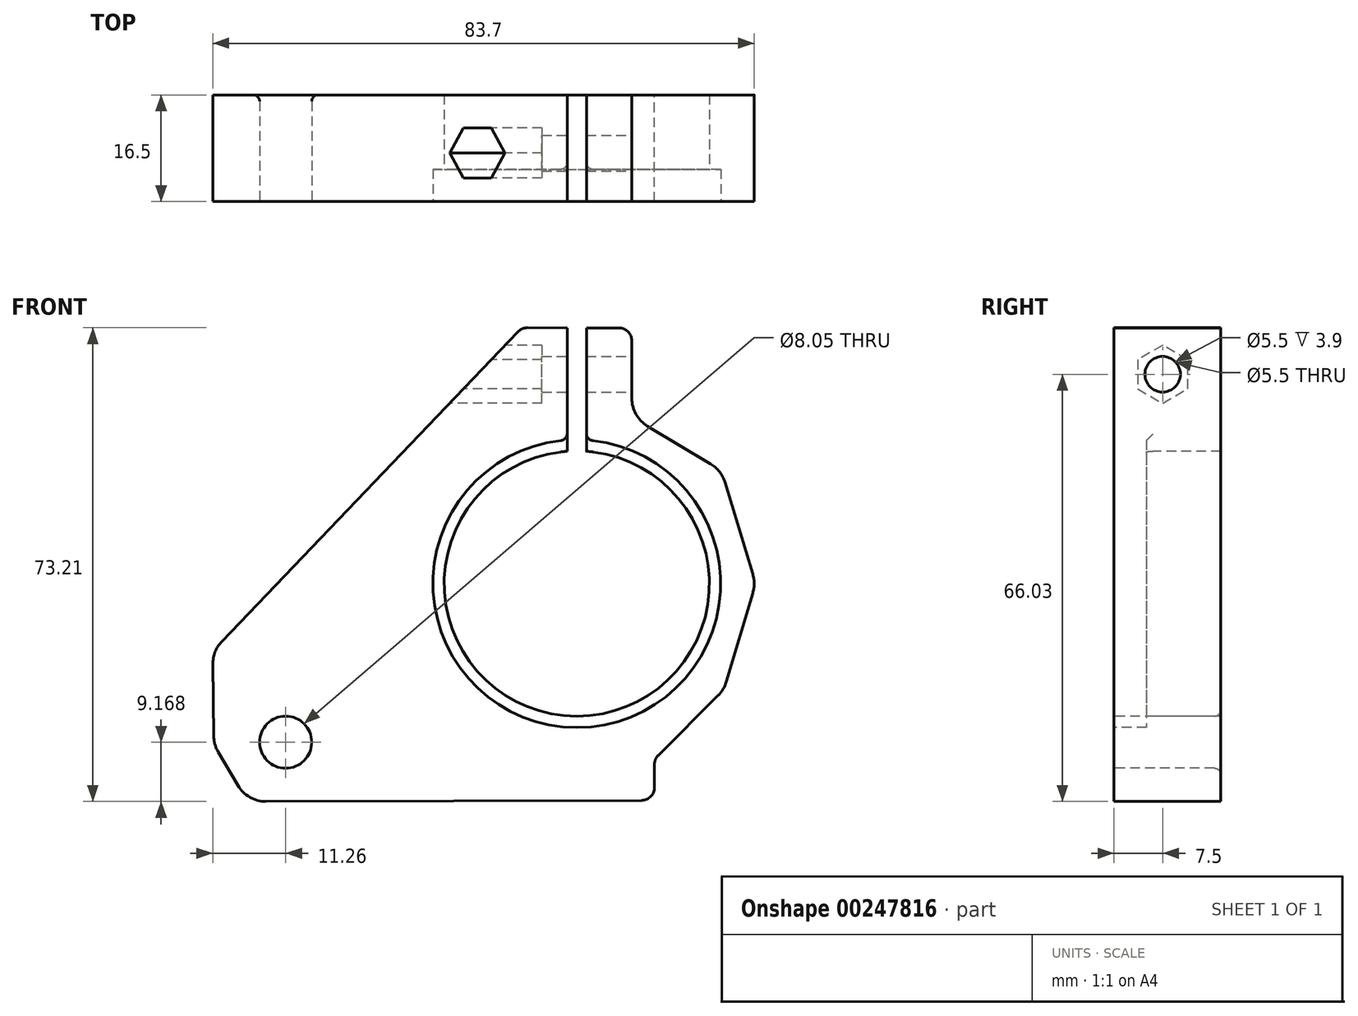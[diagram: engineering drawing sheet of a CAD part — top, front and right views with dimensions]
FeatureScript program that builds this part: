
annotation { "Feature Type Name" : "Feature", "Feature Type Description" : "" }
export const myFeature = defineFeature(function(context is Context, id is Id, definition is map)
    precondition{}
    {
        {
            var Q0;
            Q0=qCreatedBy(makeId("Front.planeOp"),FACE);
            var sketch = newSketch(context, id + "F0", { "sketchPlane" : qUnion([Q0])});
            skCircle(sketch, "E0", {"center": v(0, 0) * mm, "radius": 20.5 * mm});
            skSolve(sketch);
        }
        {
            var Q0;
            Q0=qCreatedBy(makeId("Front.planeOp"),FACE);
            var sketch = newSketch(context, id + "F1", { "sketchPlane" : qUnion([Q0])});
            skCircle(sketch, "E1", {"center": v(0, 0) * mm, "radius": 25.5 * mm});
            skSolve(sketch);
        }
        {
            var Q0;
            Q0=qCreatedBy(makeId("Front.planeOp"),FACE);
            var sketch = newSketch(context, id + "F2", { "sketchPlane" : qUnion([Q0])});
            skLineSegment(sketch, "E2.bottom", {"start": v(0, 39.5) * mm, "end": v(8.5, 39.5) * mm});
            skLineSegment(sketch, "E2.top", {"start": v(0, 20.5) * mm, "end": v(8.5, 20.5) * mm});
            skLineSegment(sketch, "E2.left", {"start": v(0, 39.5) * mm, "end": v(0, 20.5) * mm});
            skLineSegment(sketch, "E2.right", {"start": v(8.5, 39.5) * mm, "end": v(8.5, 20.5) * mm});
            skSolve(sketch);
        }
        {
            var Q0;
            Q0=qCreatedBy(makeId("Front.planeOp"),FACE);
            var sketch = newSketch(context, id + "F3", { "sketchPlane" : qUnion([Q0])});
            skLineSegment(sketch, "E3", {"start": v(-82.14, -33.5) * mm, "end": v(83.47, -33.5) * mm, "construction": true});
            skSolve(sketch);
        }
        {
            var Q0;
            Q0=qCreatedBy(makeId("Front.planeOp"),FACE);
            var sketch = newSketch(context, id + "F4", { "sketchPlane" : qUnion([Q0])});
            skLineSegment(sketch, "E4", {"start": v(12, 14.57) * mm, "end": v(12, -33.5) * mm, "construction": true});
            skSolve(sketch);
        }
        {
            var Q0;
            Q0=qCreatedBy(makeId("Front.planeOp"),FACE);
            var sketch = newSketch(context, id + "F5", { "sketchPlane" : qUnion([Q0])});
            skLineSegment(sketch, "E5", {"start": v(-54, 24.36) * mm, "end": v(-54, -39.87) * mm, "construction": true});
            skSolve(sketch);
        }
        {
            var Q0;
            Q0=qCreatedBy(makeId("Front.planeOp"),FACE);
            var sketch = newSketch(context, id + "F6", { "sketchPlane" : qUnion([Q0])});
            skLineSegment(sketch, "E6", {"start": v(-54, -28.5) * mm, "end": v(30.8, -28.5) * mm, "construction": true});
            skSolve(sketch);
        }
        {
            var Q0;
            Q0=qCreatedBy(makeId("Front.planeOp"),FACE);
            var sketch = newSketch(context, id + "F7", { "sketchPlane" : qUnion([Q0])});
            skLineSegment(sketch, "E7", {"start": v(-49, 18.78) * mm, "end": v(-49, -35.89) * mm, "construction": true});
            skSolve(sketch);
        }
        {
            var Q0;
            Q0=qCreatedBy(makeId("Front.planeOp"),FACE);
            var sketch = newSketch(context, id + "F8", { "sketchPlane" : qUnion([Q0])});
            skLineSegment(sketch, "E8", {"start": v(-49, -24.5) * mm, "end": v(12.95, -24.5) * mm, "construction": true});
            skSolve(sketch);
        }
        {
            var Q0;
            Q0=qCreatedBy(makeId("Front.planeOp"),FACE);
            var sketch = newSketch(context, id + "F9", { "sketchPlane" : qUnion([Q0])});
            skCircle(sketch, "E9", {"center": v(-45.01, -24.5) * mm, "radius": 4 * mm, "construction": true});
            skSolve(sketch);
        }
        {
            var Q0;
            Q0=qCreatedBy(makeId("Front.planeOp"),FACE);
            var sketch = newSketch(context, id + "F10", { "sketchPlane" : qUnion([Q0])});
            skCircle(sketch, "E10", {"center": v(-45.01, -24.5) * mm, "radius": 9 * mm, "construction": true});
            skSolve(sketch);
        }
        {
            var Q0;
            Q0=qCreatedBy(makeId("Front.planeOp"),FACE);
            var sketch = newSketch(context, id + "F11", { "sketchPlane" : qUnion([Q0])});
            skLineSegment(sketch, "E11", {"start": v(-44.9, -33.5) * mm, "end": v(12.01, -33.5) * mm, "construction": true});
            skLineSegment(sketch, "E12", {"start": v(12.01, -33.5) * mm, "end": v(12.01, -22.5) * mm});
            skSolve(sketch);
        }
        {
            assignVariable(context, id + "F12", {"name" : "grosor", "anyValue" : 15});
        }
        {
            var Q0;
            Q0=qCreatedBy(makeId("Front.planeOp"),FACE);
            cPlane(context, id + "F13", {"entities" : qUnion([Q0]), "cplaneType" : CPlaneType.OFFSET, "offset" : 20 * mm, "width" : 150 * mm, "height" : 150 * mm});
        }
        {
            var Q0;
            Q0=qCreatedBy(id+"F13.planeOp",FACE);
            var sketch = newSketch(context, id + "F14", { "sketchPlane" : qUnion([Q0])});
            skLineSegment(sketch, "E13", {"start": v(-8.5, 39.54) * mm, "end": v(-56.3, -10.43) * mm});
            skLineSegment(sketch, "E14", {"start": v(-56.3, -10.43) * mm, "end": v(-56.12, -24.88) * mm});
            skLineSegment(sketch, "E15", {"start": v(-56.12, -24.88) * mm, "end": v(-50.94, -33.68) * mm});
            skLineSegment(sketch, "E16", {"start": v(-50.94, -33.68) * mm, "end": v(12.01, -33.5) * mm});
            skLineSegment(sketch, "E17", {"start": v(12.01, -33.5) * mm, "end": v(12.01, -27.1) * mm});
            skLineSegment(sketch, "E18", {"start": v(12.01, -27.1) * mm, "end": v(22.74, -16.4) * mm});
            skLineSegment(sketch, "E19", {"start": v(22.74, -16.4) * mm, "end": v(27.65, 0) * mm});
            skLineSegment(sketch, "E20", {"start": v(27.65, 0) * mm, "end": v(22.34, 17.51) * mm});
            skLineSegment(sketch, "E21", {"start": v(22.34, 17.51) * mm, "end": v(8.5, 25.8) * mm});
            skLineSegment(sketch, "E22", {"start": v(8.5, 25.8) * mm, "end": v(8.5, 39.5) * mm});
            skLineSegment(sketch, "E23", {"start": v(8.5, 39.5) * mm, "end": v(-8.5, 39.54) * mm});
            skSolve(sketch);
        }
        {
            var Q0;
            Q0=makeQuery(id+"F14.imprint","IMPRINT",FACE,{"disambiguationData":[TD([[makeQuery(id+"F14.imprint","IMPRINT",EDGE,{"derivedFrom":sQuery(id+"F14.wireOp",EDGE,"E13")}),1.0]])]});
            extrude(context, id + "F15", {"entities" : qUnion([Q0]), "depth" : (getVariable(context, 'grosor') * 1.1) * mm});
        }
        {
            var Q0;
            Q0=makeQuery(id+"F15.opExtrude","CAP_FACE",FACE,{"disambiguationData":[OSD([sQuery(id+"F14.wireOp",EDGE,"E13"),sQuery(id+"F14.wireOp",EDGE,"E14"),sQuery(id+"F14.wireOp",EDGE,"nau9YeAK-7w5c-QdUc-g7JC-ZSVLRHTYuaYn"),sQuery(id+"F14.wireOp",EDGE,"E15"),sQuery(id+"F14.wireOp",EDGE,"E16"),sQuery(id+"F14.wireOp",EDGE,"E17"),sQuery(id+"F14.wireOp",EDGE,"E18"),sQuery(id+"F14.wireOp",EDGE,"E19"),sQuery(id+"F14.wireOp",EDGE,"E20"),sQuery(id+"F14.wireOp",EDGE,"E21"),sQuery(id+"F14.wireOp",EDGE,"E22"),sQuery(id+"F14.wireOp",EDGE,"E23")])],"isStart":false});
            var sketch = newSketch(context, id + "F16", { "sketchPlane" : qUnion([Q0])});
            skCircle(sketch, "E24", {"center": v(0, 0) * mm, "radius": 20.5 * mm});
            skSolve(sketch);
        }
        {
            var Q0;
            Q0=makeQuery(id+"F16.imprint","IMPRINT",FACE,{"disambiguationData":[TD([[makeQuery(id+"F16.imprint","IMPRINT",EDGE,{"derivedFrom":sQuery(id+"F16.wireOp",EDGE,"E24")}),1.0]])]});
            extrude(context, id + "F17", {"entities" : qUnion([Q0]), "operationType" : NewBodyOperationType.REMOVE, "oppositeDirection" : true, "depth" : (getVariable(context, 'grosor') * 1.1) * mm});
        }
        {
            var Q0;
            Q0=makeQuery(id+"F15.opExtrude","CAP_FACE",FACE,{"disambiguationData":[OSD([sQuery(id+"F14.wireOp",EDGE,"E13"),sQuery(id+"F14.wireOp",EDGE,"E14"),sQuery(id+"F14.wireOp",EDGE,"nau9YeAK-7w5c-QdUc-g7JC-ZSVLRHTYuaYn"),sQuery(id+"F14.wireOp",EDGE,"E15"),sQuery(id+"F14.wireOp",EDGE,"E16"),sQuery(id+"F14.wireOp",EDGE,"E17"),sQuery(id+"F14.wireOp",EDGE,"E18"),sQuery(id+"F14.wireOp",EDGE,"E19"),sQuery(id+"F14.wireOp",EDGE,"E20"),sQuery(id+"F14.wireOp",EDGE,"E21"),sQuery(id+"F14.wireOp",EDGE,"E22"),sQuery(id+"F14.wireOp",EDGE,"E23")])],"isStart":false});
            var sketch = newSketch(context, id + "F18", { "sketchPlane" : qUnion([Q0])});
            skCircle(sketch, "E25", {"center": v(-45.02, -24.51) * mm, "radius": 4.03 * mm});
            skSolve(sketch);
        }
        {
            var Q0;
            Q0=makeQuery(id+"F18.imprint","IMPRINT",FACE,{"disambiguationData":[TD([[makeQuery(id+"F18.imprint","IMPRINT",EDGE,{"derivedFrom":sQuery(id+"F18.wireOp",EDGE,"E25")}),1.0]])]});
            extrude(context, id + "F19", {"entities" : qUnion([Q0]), "operationType" : NewBodyOperationType.REMOVE, "oppositeDirection" : true, "depth" : (getVariable(context, 'grosor') * 1.1) * mm});
        }
        {
            var Q0;
            Q0=makeQuery(id+"F15.opExtrude","CAP_FACE",FACE,{"disambiguationData":[OSD([sQuery(id+"F14.wireOp",EDGE,"E13"),sQuery(id+"F14.wireOp",EDGE,"E14"),sQuery(id+"F14.wireOp",EDGE,"nau9YeAK-7w5c-QdUc-g7JC-ZSVLRHTYuaYn"),sQuery(id+"F14.wireOp",EDGE,"E15"),sQuery(id+"F14.wireOp",EDGE,"E16"),sQuery(id+"F14.wireOp",EDGE,"E17"),sQuery(id+"F14.wireOp",EDGE,"E18"),sQuery(id+"F14.wireOp",EDGE,"E19"),sQuery(id+"F14.wireOp",EDGE,"E20"),sQuery(id+"F14.wireOp",EDGE,"E21"),sQuery(id+"F14.wireOp",EDGE,"E22"),sQuery(id+"F14.wireOp",EDGE,"E23")])],"isStart":false});
            var sketch = newSketch(context, id + "F20", { "sketchPlane" : qUnion([Q0])});
            skLineSegment(sketch, "E26.bottom", {"start": v(1.5, 20.45) * mm, "end": v(-1.5, 20.45) * mm});
            skLineSegment(sketch, "E26.top", {"start": v(1.5, 40.45) * mm, "end": v(-1.5, 40.45) * mm});
            skLineSegment(sketch, "E26.left", {"start": v(1.5, 20.45) * mm, "end": v(1.5, 40.45) * mm});
            skLineSegment(sketch, "E26.right", {"start": v(-1.5, 20.45) * mm, "end": v(-1.5, 40.45) * mm});
            skPoint(sketch, "E26.middle", {"position": v(0, 30.45) * mm});
            skSolve(sketch);
        }
        {
            var Q0;
            Q0 = qSketchRegion(id + "F20", true);
            extrude(context, id + "F21", {"entities" : qUnion([Q0]), "operationType" : NewBodyOperationType.REMOVE, "oppositeDirection" : true, "depth" : (getVariable(context, 'grosor') * 1.1) * mm});
        }
        {
            var Q0;
            Q0=makeQuery(id+"F15.opExtrude","SWEPT_FACE",FACE,{"disambiguationData":[OSD([sQuery(id+"F14.wireOp",EDGE,"E22")])]});
            var sketch = newSketch(context, id + "F22", { "sketchPlane" : qUnion([Q0])});
            skCircle(sketch, "E27", {"center": v(-29, 32.35) * mm, "radius": 2.75 * mm});
            skSolve(sketch);
        }
        {
            var Q0;
            Q0=makeQuery(id+"F22.imprint","IMPRINT",FACE,{"disambiguationData":[TD([[makeQuery(id+"F22.imprint","IMPRINT",EDGE,{"derivedFrom":sQuery(id+"F22.wireOp",EDGE,"E27")}),1.0]])]});
            extrude(context, id + "F23", {"entities" : qUnion([Q0]), "operationType" : NewBodyOperationType.REMOVE, "oppositeDirection" : true, "depth" : 40 * mm});
        }
        {
            var Q0;
            Q0=qCreatedBy(makeId("Right.planeOp"),FACE);
            cPlane(context, id + "F24", {"entities" : qUnion([Q0]), "cplaneType" : CPlaneType.OFFSET, "offset" : 36.7 * mm, "oppositeDirection" : true, "width" : 150 * mm, "height" : 150 * mm});
        }
        {
            var Q0;
            Q0=qCreatedBy(id+"F24.planeOp",FACE);
            var sketch = newSketch(context, id + "F25", { "sketchPlane" : qUnion([Q0])});
            skCircle(sketch, "E28.cCircle", {"center": v(-29, 32.35) * mm, "radius": 3.88 * mm, "construction": true});
            skLineSegment(sketch, "E28.0", {"start": v(-32.88, 30.11) * mm, "end": v(-32.88, 34.59) * mm});
            skLineSegment(sketch, "E28.1", {"start": v(-32.88, 34.59) * mm, "end": v(-29, 36.82) * mm});
            skLineSegment(sketch, "E28.2", {"start": v(-29, 36.82) * mm, "end": v(-25.13, 34.59) * mm});
            skLineSegment(sketch, "E28.3", {"start": v(-25.13, 34.59) * mm, "end": v(-25.13, 30.11) * mm});
            skLineSegment(sketch, "E28.4", {"start": v(-25.12, 30.11) * mm, "end": v(-29, 27.88) * mm});
            skLineSegment(sketch, "E28.5", {"start": v(-29, 27.88) * mm, "end": v(-32.88, 30.11) * mm});
            skPoint(sketch, "E28.0.midPoint", {"position": v(-32.88, 32.35) * mm});
            skSolve(sketch);
        }
        {
            var Q0;
            Q0=makeQuery(id+"F25.imprint","IMPRINT",FACE,{"disambiguationData":[TD([[makeQuery(id+"F25.imprint","IMPRINT",EDGE,{"derivedFrom":sQuery(id+"F25.wireOp",EDGE,"E28.0")}),-1.0]])]});
            var Q1;
            Q1=sQuery(id+"F1.wireOp",EDGE,"E1");
            extrude(context, id + "F26", {"entities" : qUnion([Q0]), "operationType" : NewBodyOperationType.REMOVE, "surfaceEntities" : qUnion([Q1]), "depth" : 31.3 * mm});
        }
        {
            var Q0;
            Q0=makeQuery(id+"F15.opExtrude","CAP_FACE",FACE,{"disambiguationData":[OSD([sQuery(id+"F14.wireOp",EDGE,"E13"),sQuery(id+"F14.wireOp",EDGE,"E14"),sQuery(id+"F14.wireOp",EDGE,"nau9YeAK-7w5c-QdUc-g7JC-ZSVLRHTYuaYn"),sQuery(id+"F14.wireOp",EDGE,"E15"),sQuery(id+"F14.wireOp",EDGE,"E16"),sQuery(id+"F14.wireOp",EDGE,"E17"),sQuery(id+"F14.wireOp",EDGE,"E18"),sQuery(id+"F14.wireOp",EDGE,"E19"),sQuery(id+"F14.wireOp",EDGE,"E20"),sQuery(id+"F14.wireOp",EDGE,"E21"),sQuery(id+"F14.wireOp",EDGE,"E22"),sQuery(id+"F14.wireOp",EDGE,"E23")])],"isStart":false});
            var sketch = newSketch(context, id + "F27", { "sketchPlane" : qUnion([Q0])});
            skCircle(sketch, "E29", {"center": v(0, 0) * mm, "radius": 22.25 * mm});
            skSolve(sketch);
        }
        {
            var Q0;
            Q0 = qSketchRegion(id + "F27", true);
            extrude(context, id + "F28", {"entities" : qUnion([Q0]), "operationType" : NewBodyOperationType.REMOVE, "oppositeDirection" : true, "depth" : 5 * mm});
        }
        {
            var Q0;
            Q0=makeQuery(id+"F19.boolean.opBoolean","COPY",EDGE,{"derivedFrom":makeQuery(id+"F19.opExtrude","CAP_EDGE",EDGE,{"disambiguationData":[OSD([sQuery(id+"F18.wireOp",EDGE,"E25")])],"isStart":true})});
            var Q1;
            Q1=makeQuery(id+"F19.boolean.opBoolean","INTERSECT",EDGE,{"derivedFrom":[makeQuery(id+"F15.opExtrude","CAP_FACE",FACE,{"disambiguationData":[OSD([sQuery(id+"F14.wireOp",EDGE,"E13"),sQuery(id+"F14.wireOp",EDGE,"E14"),sQuery(id+"F14.wireOp",EDGE,"nau9YeAK-7w5c-QdUc-g7JC-ZSVLRHTYuaYn"),sQuery(id+"F14.wireOp",EDGE,"E15"),sQuery(id+"F14.wireOp",EDGE,"E16"),sQuery(id+"F14.wireOp",EDGE,"E17"),sQuery(id+"F14.wireOp",EDGE,"E18"),sQuery(id+"F14.wireOp",EDGE,"E19"),sQuery(id+"F14.wireOp",EDGE,"E20"),sQuery(id+"F14.wireOp",EDGE,"E21"),sQuery(id+"F14.wireOp",EDGE,"E22"),sQuery(id+"F14.wireOp",EDGE,"E23")])],"isStart":true}),makeQuery(id+"F19.opExtrude","SWEPT_FACE",FACE,{"disambiguationData":[OSD([sQuery(id+"F18.wireOp",EDGE,"E25")])]})]});
            fillet(context, id + "F29", {"entities" : qUnion([Q0, Q1]), "radius" : 1 * mm, "tangentPropagation" : true, "allowEdgeOverflow" : false});
        }
        {
            var Q0;
            Q0=makeQuery(id+"F15.opExtrude","SWEPT_EDGE",EDGE,{"disambiguationData":[OSD([sQuery(id+"F14.wireOp",EDGE,"E19"),sQuery(id+"F14.wireOp",EDGE,"E20")])]});
            fillet(context, id + "F30", {"entities" : qUnion([Q0]), "radius" : 5 * mm, "tangentPropagation" : true, "allowEdgeOverflow" : false});
        }
        {
            var Q0;
            Q0=makeQuery(id+"F15.opExtrude","SWEPT_EDGE",EDGE,{"disambiguationData":[OSD([sQuery(id+"F14.wireOp",EDGE,"E20"),sQuery(id+"F14.wireOp",EDGE,"E21")])]});
            fillet(context, id + "F31", {"entities" : qUnion([Q0]), "radius" : 5 * mm, "tangentPropagation" : true, "allowEdgeOverflow" : false});
        }
        {
            var Q0;
            Q0=makeQuery(id+"F15.opExtrude","SWEPT_EDGE",EDGE,{"disambiguationData":[OSD([sQuery(id+"F14.wireOp",EDGE,"E18"),sQuery(id+"F14.wireOp",EDGE,"E19")])]});
            fillet(context, id + "F32", {"entities" : qUnion([Q0]), "radius" : 5 * mm, "tangentPropagation" : true, "allowEdgeOverflow" : false});
        }
        {
            var Q0;
            Q0=makeQuery(id+"F15.opExtrude","SWEPT_EDGE",EDGE,{"disambiguationData":[OSD([sQuery(id+"F14.wireOp",EDGE,"E21"),sQuery(id+"F14.wireOp",EDGE,"E22")])]});
            fillet(context, id + "F33", {"entities" : qUnion([Q0]), "radius" : 5 * mm, "tangentPropagation" : true, "allowEdgeOverflow" : false});
        }
        {
            var Q0;
            Q0=makeQuery(id+"F15.opExtrude","SWEPT_EDGE",EDGE,{"disambiguationData":[OSD([sQuery(id+"F14.wireOp",EDGE,"E15"),sQuery(id+"F14.wireOp",EDGE,"E16")])]});
            var Q1;
            Q1=makeQuery(id+"F15.opExtrude","SWEPT_EDGE",EDGE,{"disambiguationData":[OSD([sQuery(id+"F14.wireOp",EDGE,"E14"),sQuery(id+"F14.wireOp",EDGE,"E15")])]});
            var Q2;
            Q2=makeQuery(id+"F15.opExtrude","SWEPT_EDGE",EDGE,{"disambiguationData":[OSD([sQuery(id+"F14.wireOp",EDGE,"E13"),sQuery(id+"F14.wireOp",EDGE,"E14")])]});
            fillet(context, id + "F34", {"entities" : qUnion([Q0, Q1, Q2]), "radius" : 5 * mm, "tangentPropagation" : true, "allowEdgeOverflow" : false});
        }
        {
            var Q0;
            Q0=makeQuery(id+"F15.opExtrude","SWEPT_EDGE",EDGE,{"disambiguationData":[OSD([sQuery(id+"F14.wireOp",EDGE,"E16"),sQuery(id+"F14.wireOp",EDGE,"E17")])]});
            var Q1;
            Q1=makeQuery(id+"F15.opExtrude","SWEPT_EDGE",EDGE,{"disambiguationData":[OSD([sQuery(id+"F14.wireOp",EDGE,"E17"),sQuery(id+"F14.wireOp",EDGE,"E18")])]});
            fillet(context, id + "F35", {"entities" : qUnion([Q0, Q1]), "radius" : 2 * mm, "tangentPropagation" : true, "allowEdgeOverflow" : false});
        }
        {
            var Q0;
            Q0=makeQuery(id+"F15.opExtrude","SWEPT_EDGE",EDGE,{"disambiguationData":[OSD([sQuery(id+"F14.wireOp",EDGE,"E13"),sQuery(id+"F14.wireOp",EDGE,"E23")])]});
            var Q1;
            Q1=makeQuery(id+"F15.opExtrude","SWEPT_EDGE",EDGE,{"disambiguationData":[OSD([sQuery(id+"F14.wireOp",EDGE,"E22"),sQuery(id+"F14.wireOp",EDGE,"E23")])]});
            fillet(context, id + "F36", {"entities" : qUnion([Q0, Q1]), "radius" : 2 * mm, "tangentPropagation" : true, "allowEdgeOverflow" : false});
        }
        {
            var Q0;
            Q0=makeQuery(id+"F21.boolean.opBoolean","COPY",EDGE,{"derivedFrom":makeQuery(id+"F21.opExtrude","SWEPT_EDGE",EDGE,{"disambiguationData":[OSD([sQuery(id+"F16.wireOp",EDGE,"E24"),sQuery(id+"F20.wireOp",EDGE,"E26.bottom"),sQuery(id+"F20.wireOp",EDGE,"E26.right")])]})});
            var Q1;
            Q1=makeQuery(id+"F28.boolean.opBoolean","INTERSECT",EDGE,{"derivedFrom":[makeQuery(id+"F21.boolean.opBoolean","COPY",FACE,{"derivedFrom":makeQuery(id+"F21.opExtrude","SWEPT_FACE",FACE,{"disambiguationData":[OSD([sQuery(id+"F20.wireOp",EDGE,"E26.right")])]})}),makeQuery(id+"F28.opExtrude","SWEPT_FACE",FACE,{"disambiguationData":[OSD([sQuery(id+"F27.wireOp",EDGE,"E29")])]})]});
            var Q2;
            Q2=makeQuery(id+"F21.boolean.opBoolean","COPY",EDGE,{"derivedFrom":makeQuery(id+"F21.opExtrude","SWEPT_EDGE",EDGE,{"disambiguationData":[OSD([sQuery(id+"F16.wireOp",EDGE,"E24"),sQuery(id+"F20.wireOp",EDGE,"E26.bottom"),sQuery(id+"F20.wireOp",EDGE,"E26.left")])]})});
            var Q3;
            Q3=makeQuery(id+"F28.boolean.opBoolean","INTERSECT",EDGE,{"derivedFrom":[makeQuery(id+"F21.boolean.opBoolean","COPY",FACE,{"derivedFrom":makeQuery(id+"F21.opExtrude","SWEPT_FACE",FACE,{"disambiguationData":[OSD([sQuery(id+"F20.wireOp",EDGE,"E26.left")])]})}),makeQuery(id+"F28.opExtrude","CAP_FACE",FACE,{"disambiguationData":[OSD([sQuery(id+"F27.wireOp",EDGE,"E29")])],"isStart":false})]});
            var Q4;
            Q4=makeQuery(id+"F28.boolean.opBoolean","INTERSECT",EDGE,{"derivedFrom":[makeQuery(id+"F21.boolean.opBoolean","COPY",FACE,{"derivedFrom":makeQuery(id+"F21.opExtrude","SWEPT_FACE",FACE,{"disambiguationData":[OSD([sQuery(id+"F20.wireOp",EDGE,"E26.left")])]})}),makeQuery(id+"F28.opExtrude","SWEPT_FACE",FACE,{"disambiguationData":[OSD([sQuery(id+"F27.wireOp",EDGE,"E29")])]})]});
            var Q5;
            Q5=makeQuery(id+"F28.boolean.opBoolean","INTERSECT",EDGE,{"derivedFrom":[makeQuery(id+"F21.boolean.opBoolean","COPY",FACE,{"derivedFrom":makeQuery(id+"F21.opExtrude","SWEPT_FACE",FACE,{"disambiguationData":[OSD([sQuery(id+"F20.wireOp",EDGE,"E26.right")])]})}),makeQuery(id+"F28.opExtrude","CAP_FACE",FACE,{"disambiguationData":[OSD([sQuery(id+"F27.wireOp",EDGE,"E29")])],"isStart":false})]});
            var Q6;
            Q6=makeQuery(id+"F21.boolean.opBoolean","COPY",EDGE,{"derivedFrom":makeQuery(id+"F21.opExtrude","CAP_EDGE",EDGE,{"disambiguationData":[OSD([sQuery(id+"F20.wireOp",EDGE,"E26.right")])],"isStart":false})});
            var Q7;
            Q7=makeQuery(id+"F21.boolean.opBoolean","COPY",EDGE,{"derivedFrom":makeQuery(id+"F21.opExtrude","CAP_EDGE",EDGE,{"disambiguationData":[OSD([sQuery(id+"F20.wireOp",EDGE,"E26.left")])],"isStart":false})});
            fillet(context, id + "F37", {"entities" : qUnion([Q0, Q1, Q2, Q3, Q4, Q5, Q6, Q7]), "radius" : 1 * mm, "tangentPropagation" : true, "allowEdgeOverflow" : false});
        }
    });
